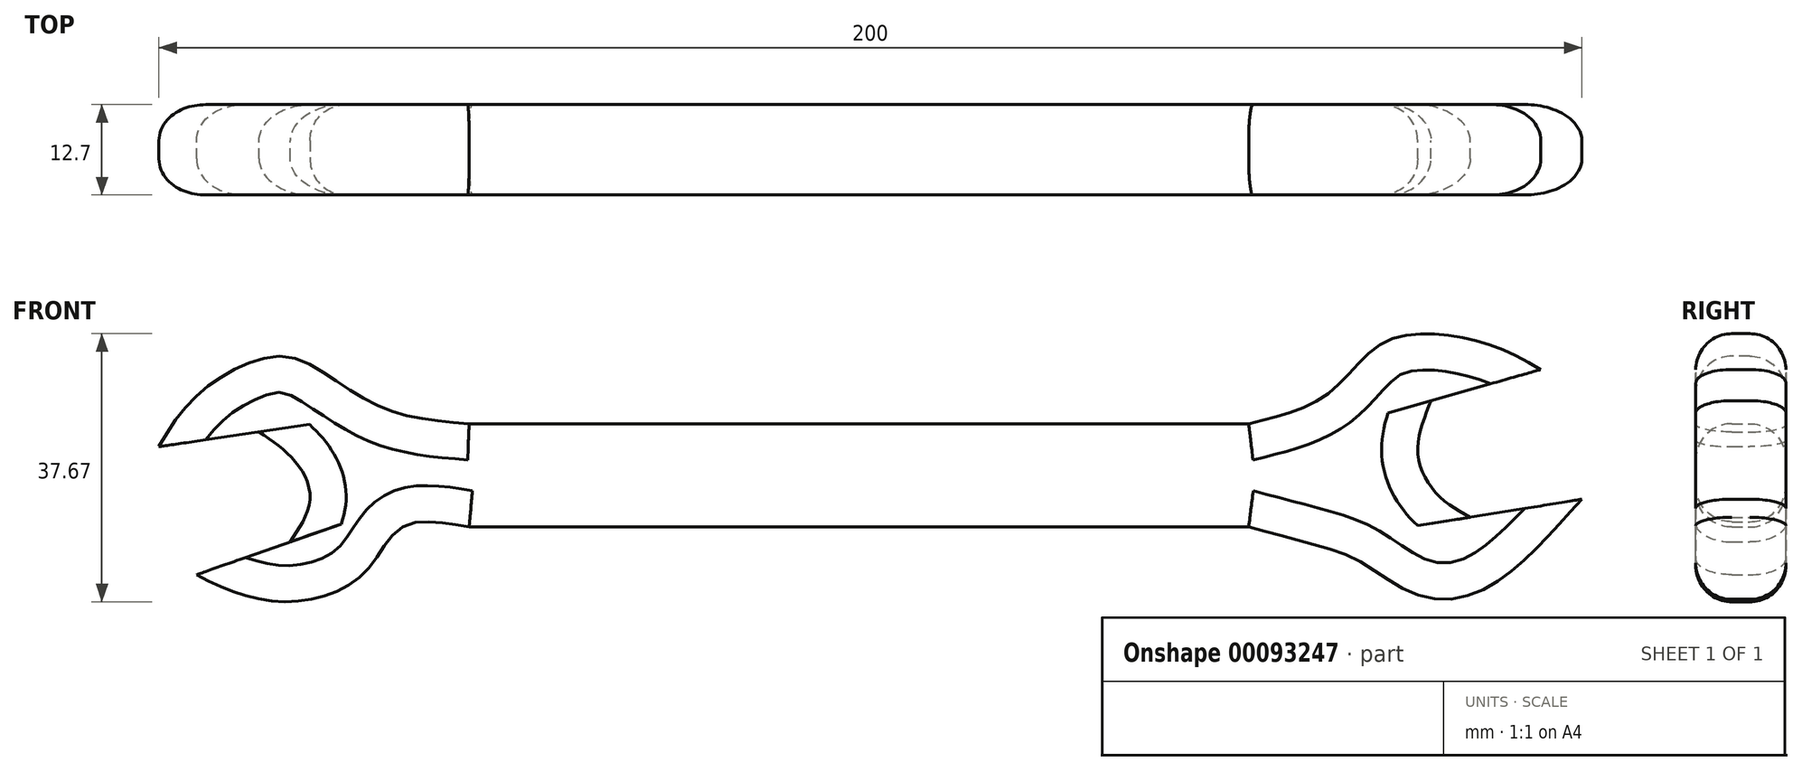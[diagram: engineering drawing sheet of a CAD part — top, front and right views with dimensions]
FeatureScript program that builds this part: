
annotation { "Feature Type Name" : "Feature", "Feature Type Description" : "" }
export const myFeature = defineFeature(function(context is Context, id is Id, definition is map)
    precondition{}
    {
        {
            var Q0;
            Q0=qCreatedBy(makeId("Front.planeOp"),FACE);
            var sketch = newSketch(context, id + "F0", { "sketchPlane" : qUnion([Q0])});
            skLineSegment(sketch, "E0", {"start": v(-53.94, 7.31) * mm, "end": v(55.63, 7.31) * mm});
            skLineSegment(sketch, "E1", {"start": v(-53.94, -7.22) * mm, "end": v(55.63, -7.22) * mm});
            skFitSpline(sketch, "E2", {"points": [v(-53.94, 7.31) * mm, v(-65.7, 9.39) * mm, v(-74.7, 14.7) * mm, v(-81.16, 16.77) * mm, v(-91.77, 11.7) * mm, v(-97.54, 4.08) * mm], "startDerivative": vector(-55.88, 4.44) * mm, "endDerivative": vector(-23.72, -40.5) * mm});
            skFitSpline(sketch, "E3", {"points": [v(-53.94, -7.22) * mm, v(-63.4, -7.22) * mm, v(-68.7, -13.68) * mm, v(-81.62, -17.6) * mm, v(-92.24, -13.9) * mm, v(-92.93, -13.45) * mm], "startDerivative": vector(-48.85, 8.93) * mm, "endDerivative": vector(-6.97, 5.34) * mm});
            skLineSegment(sketch, "E4", {"start": v(-97.54, 4.08) * mm, "end": v(-83.47, 6.16) * mm});
            skLineSegment(sketch, "E5", {"start": v(-92.24, -13.9) * mm, "end": v(-79.09, -9.3) * mm});
            skFitSpline(sketch, "E6", {"points": [v(-83.47, 6.16) * mm, v(-78.4, 2) * mm, v(-76.32, -3.3) * mm, v(-79.09, -9.3) * mm], "startDerivative": vector(16.23, -11) * mm, "endDerivative": vector(-11.57, -17.47) * mm});
            skFitSpline(sketch, "E7", {"points": [v(55.63, 7.31) * mm, v(63.94, 9.85) * mm, v(69.24, 13.77) * mm, v(75.93, 19.3) * mm, v(89.54, 18.39) * mm, v(96.7, 14.93) * mm], "startDerivative": vector(45.17, 10.91) * mm, "endDerivative": vector(32.56, -19.55) * mm});
            skFitSpline(sketch, "E8", {"points": [v(55.63, -7.22) * mm, v(66.01, -9.99) * mm, v(71.32, -12.06) * mm, v(79.16, -16.68) * mm, v(88.62, -15.99) * mm, v(102.46, -3.3) * mm], "startDerivative": vector(55.9, -14.6) * mm, "endDerivative": vector(51.6, 57.96) * mm});
            skFitSpline(sketch, "E9", {"points": [v(81.24, 10.54) * mm, v(79.4, 4.08) * mm, v(80.31, 0) * mm, v(82.85, -3.3) * mm, v(86.77, -5.84) * mm], "startDerivative": vector(-8.89, -23.14) * mm, "endDerivative": vector(17.08, -9.48) * mm});
            skLineSegment(sketch, "E10", {"start": v(96.7, 14.93) * mm, "end": v(81.24, 10.54) * mm});
            skLineSegment(sketch, "E11", {"start": v(102.46, -3.3) * mm, "end": v(86.77, -5.84) * mm});
            skSolve(sketch);
        }
        {
            var Q0;
            Q0=makeQuery(id+"F0.imprint","IMPRINT",FACE,{"disambiguationData":[TD([[makeQuery(id+"F0.imprint","IMPRINT",EDGE,{"derivedFrom":sQuery(id+"F0.wireOp",EDGE,"E0")}),-1.0]])]});
            extrude(context, id + "F1", {"entities" : qUnion([Q0]), "depth" : 6.35 * mm});
        }
        {
            var Q0;
            Q0=makeQuery(id+"F1.opExtrude","CAP_EDGE",EDGE,{"disambiguationData":[OSD([sQuery(id+"F0.wireOp",EDGE,"E3")])],"isStart":false});
            var Q1;
            Q1=makeQuery(id+"F1.opExtrude","CAP_EDGE",EDGE,{"disambiguationData":[OSD([sQuery(id+"F0.wireOp",EDGE,"E6")])],"isStart":false});
            var Q2;
            Q2=makeQuery(id+"F1.opExtrude","CAP_EDGE",EDGE,{"disambiguationData":[OSD([sQuery(id+"F0.wireOp",EDGE,"E2")])],"isStart":false});
            var Q3;
            Q3=makeQuery(id+"F1.opExtrude","CAP_EDGE",EDGE,{"disambiguationData":[OSD([sQuery(id+"F0.wireOp",EDGE,"E0")])],"isStart":false});
            var Q4;
            Q4=makeQuery(id+"F1.opExtrude","CAP_EDGE",EDGE,{"disambiguationData":[OSD([sQuery(id+"F0.wireOp",EDGE,"E1")])],"isStart":false});
            var Q5;
            Q5=makeQuery(id+"F1.opExtrude","CAP_EDGE",EDGE,{"disambiguationData":[OSD([sQuery(id+"F0.wireOp",EDGE,"E8")])],"isStart":false});
            var Q6;
            Q6=makeQuery(id+"F1.opExtrude","CAP_EDGE",EDGE,{"disambiguationData":[OSD([sQuery(id+"F0.wireOp",EDGE,"E7")])],"isStart":false});
            var Q7;
            Q7=makeQuery(id+"F1.opExtrude","CAP_EDGE",EDGE,{"disambiguationData":[OSD([sQuery(id+"F0.wireOp",EDGE,"E9")])],"isStart":false});
            fillet(context, id + "F2", {"entities" : qUnion([Q0, Q1, Q2, Q3, Q4, Q5, Q6, Q7]), "radius" : 5.08 * mm, "tangentPropagation" : true, "allowEdgeOverflow" : false});
        }
        {
            var Q0;
            Q0=makeQuery(id+"F1.opExtrude","SWEPT_BODY",BODY,{"disambiguationData":[OSD([sQuery(id+"F0.wireOp",EDGE,"E0"),sQuery(id+"F0.wireOp",EDGE,"E1"),sQuery(id+"F0.wireOp",EDGE,"E2"),sQuery(id+"F0.wireOp",EDGE,"E3"),sQuery(id+"F0.wireOp",EDGE,"E4"),sQuery(id+"F0.wireOp",EDGE,"E5"),sQuery(id+"F0.wireOp",EDGE,"E6"),sQuery(id+"F0.wireOp",EDGE,"E7"),sQuery(id+"F0.wireOp",EDGE,"E8"),sQuery(id+"F0.wireOp",EDGE,"E9"),sQuery(id+"F0.wireOp",EDGE,"E10"),sQuery(id+"F0.wireOp",EDGE,"E11")])]});
            var Q1;
            Q1=qCreatedBy(makeId("Front.planeOp"),FACE);
            mirror(context, id + "F3", {"operationType" : NewBodyOperationType.ADD, "entities" : qUnion([Q0]), "mirrorPlane" : qUnion([Q1])});
        }
    });
